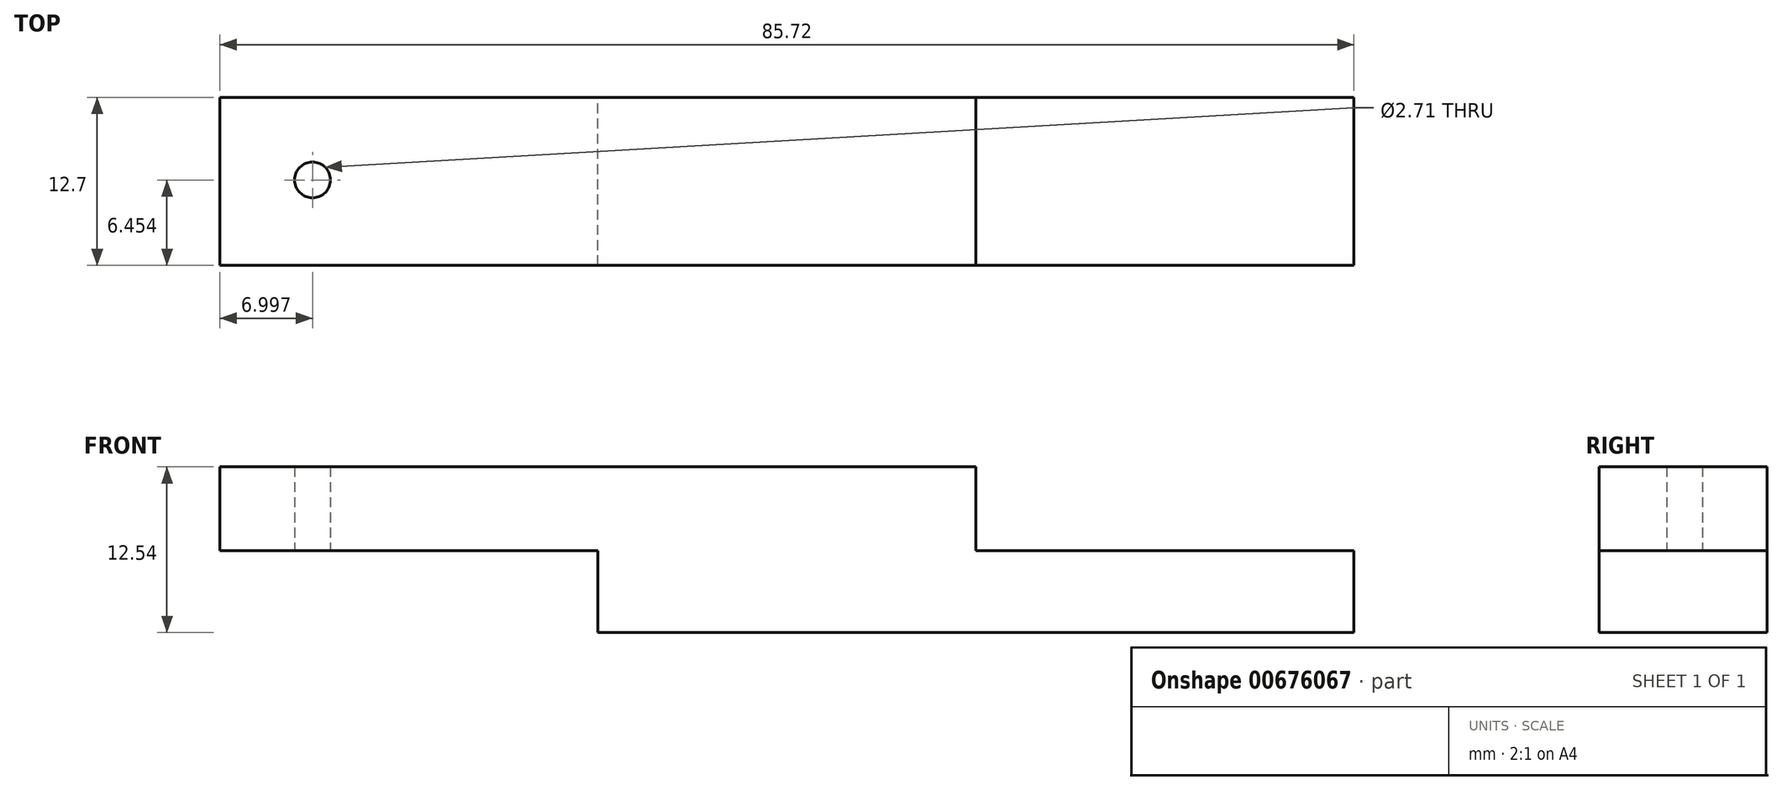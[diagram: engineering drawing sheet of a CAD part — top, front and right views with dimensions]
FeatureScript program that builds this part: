
annotation { "Feature Type Name" : "Feature", "Feature Type Description" : "" }
export const myFeature = defineFeature(function(context is Context, id is Id, definition is map)
    precondition{}
    {
        {
            var Q0;
            Q0=qCreatedBy(makeId("Front.planeOp"),FACE);
            var sketch = newSketch(context, id + "F0", { "sketchPlane" : qUnion([Q0])});
            skLineSegment(sketch, "E0.bottom", {"start": v(-18.17, 29.65) * mm, "end": v(38.98, 29.65) * mm});
            skLineSegment(sketch, "E0.top", {"start": v(-18.17, 23.3) * mm, "end": v(38.98, 23.3) * mm});
            skLineSegment(sketch, "E0.left", {"start": v(-18.17, 29.65) * mm, "end": v(-18.17, 23.3) * mm});
            skLineSegment(sketch, "E0.right", {"start": v(38.98, 29.65) * mm, "end": v(38.98, 23.3) * mm});
            skLineSegment(sketch, "E1.bottom", {"start": v(10.4, 23.3) * mm, "end": v(67.55, 23.3) * mm});
            skLineSegment(sketch, "E1.top", {"start": v(10.4, 17.1) * mm, "end": v(67.55, 17.1) * mm});
            skLineSegment(sketch, "E1.left", {"start": v(10.4, 23.3) * mm, "end": v(10.4, 17.1) * mm});
            skLineSegment(sketch, "E1.right", {"start": v(67.55, 23.3) * mm, "end": v(67.55, 17.1) * mm});
            skSolve(sketch);
        }
        {
            var Q0;
            Q0 = qSketchRegion(id + "F0", true);
            extrude(context, id + "F1", {"entities" : qUnion([Q0]), "depth" : 12.7 * mm, "offsetDistance" : 25.4 * mm});
        }
        {
            var Q0;
            Q0=qCreatedBy(makeId("Top.planeOp"),FACE);
            var sketch = newSketch(context, id + "F2", { "sketchPlane" : qUnion([Q0])});
            skCircle(sketch, "E2", {"center": v(-11.17, -6.25) * mm, "radius": 1.35 * mm});
            skSolve(sketch);
        }
        {
            var Q0;
            Q0 = qSketchRegion(id + "F2", true);
            extrude(context, id + "F3", {"entities" : qUnion([Q0]), "operationType" : NewBodyOperationType.REMOVE, "depth" : 50.8 * mm, "offsetDistance" : 25.4 * mm});
        }
    });
